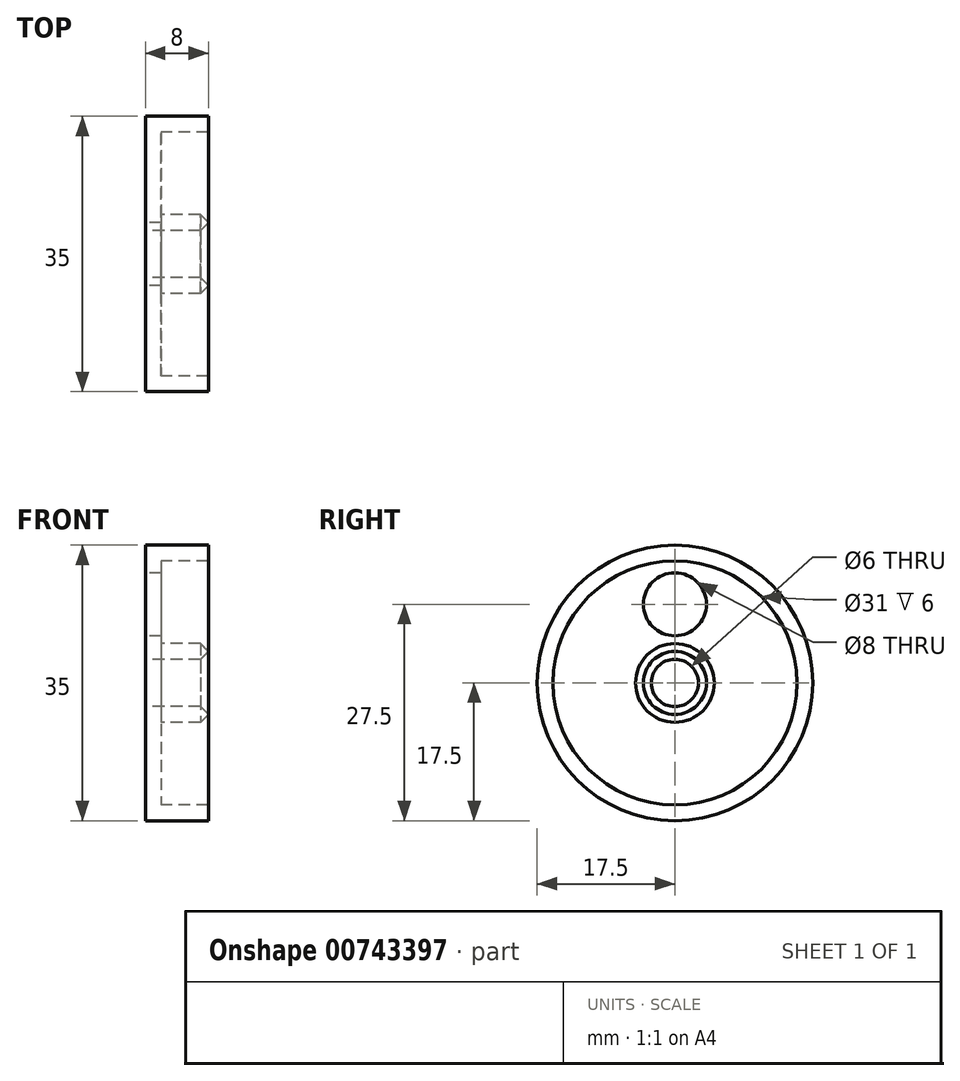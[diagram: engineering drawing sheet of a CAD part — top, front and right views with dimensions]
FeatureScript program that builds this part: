
annotation { "Feature Type Name" : "Feature", "Feature Type Description" : "" }
export const myFeature = defineFeature(function(context is Context, id is Id, definition is map)
    precondition{}
    {
        {
            var Q0;
            Q0=qCreatedBy(makeId("Front.planeOp"),FACE);
            var sketch = newSketch(context, id + "F0", { "sketchPlane" : qUnion([Q0])});
            skLineSegment(sketch, "E0.bottom", {"start": v(0, 0) * mm, "end": v(8, 0) * mm});
            skLineSegment(sketch, "E0.top", {"start": v(0, 17.5) * mm, "end": v(8, 17.5) * mm});
            skLineSegment(sketch, "E0.left", {"start": v(0, 0) * mm, "end": v(0, 17.5) * mm});
            skLineSegment(sketch, "E0.right", {"start": v(8, 0) * mm, "end": v(8, 17.5) * mm});
            skSolve(sketch);
        }
        {
            var Q0;
            Q0 = qSketchRegion(id + "F0", true);
            var Q1;
            Q1=sQuery(id+"F0.wireOp",EDGE,"E0.bottom");
            revolve(context, id + "F1", {"surfaceOperationType" : NewSurfaceOperationType.NEW, "entities" : qUnion([Q0]), "axis" : qUnion([Q1]), "revolveType" : RevolveType.FULL});
        }
        {
            var Q0;
            Q0=qCreatedBy(makeId("Right.planeOp"),FACE);
            var sketch = newSketch(context, id + "F2", { "sketchPlane" : qUnion([Q0])});
            skPoint(sketch, "E1", {"position": v(0, 0) * mm});
            skSolve(sketch);
        }
        {
            var Q0;
            Q0=sQuery(id+"F2.wireOp",VERTEX,"E1");
            var Q1;
            Q1=makeQuery(id+"F1.opRevolve","SWEPT_BODY",BODY,{"disambiguationData":[OSD([sQuery(id+"F0.wireOp",EDGE,"E0.bottom"),sQuery(id+"F0.wireOp",EDGE,"E0.top"),sQuery(id+"F0.wireOp",EDGE,"E0.left"),sQuery(id+"F0.wireOp",EDGE,"E0.right")])]});
            hole(context, id + "F3", {"style" : HoleStyle.SIMPLE, "endStyle" : HoleEndStyle.THROUGH, "oppositeDirection" : true, "holeDiameter" : 6 * mm, "majorDiameter" : 5 * mm, "isTappedThrough" : true, "tappedDepth" : 12 * mm, "tapClearance" : 3, "locations" : qUnion([Q0]), "scope" : qUnion([Q1])});
        }
        {
            var Q0;
            Q0=makeQuery(id+"F1.opRevolve","SWEPT_FACE",FACE,{"disambiguationData":[OSD([sQuery(id+"F0.wireOp",EDGE,"E0.right")])]});
            shell(context, id + "F4", {"entities" : qUnion([Q0]), "thickness" : 2 * mm});
        }
        {
            var Q0;
            Q0=qCreatedBy(makeId("Right.planeOp"),FACE);
            var sketch = newSketch(context, id + "F5", { "sketchPlane" : qUnion([Q0])});
            skPoint(sketch, "E2", {"position": v(0, 10) * mm});
            skSolve(sketch);
        }
        {
            var Q0;
            Q0=sQuery(id+"F5.wireOp",VERTEX,"E2");
            var Q1;
            Q1=makeQuery(id+"F1.opRevolve","SWEPT_BODY",BODY,{"disambiguationData":[OSD([sQuery(id+"F0.wireOp",EDGE,"E0.bottom"),sQuery(id+"F0.wireOp",EDGE,"E0.top"),sQuery(id+"F0.wireOp",EDGE,"E0.left"),sQuery(id+"F0.wireOp",EDGE,"E0.right")])]});
            hole(context, id + "F6", {"style" : HoleStyle.SIMPLE, "endStyle" : HoleEndStyle.THROUGH, "oppositeDirection" : true, "holeDiameter" : 8 * mm, "majorDiameter" : 5 * mm, "isTappedThrough" : true, "tappedDepth" : 12 * mm, "tapClearance" : 3, "locations" : qUnion([Q0]), "scope" : qUnion([Q1])});
        }
        {
            var Q0;
            Q0=makeQuery(id+"F4.opShell","OFFSET_FACE",FACE,{"disambiguationData":[OSD([sQuery(id+"F0.wireOp",EDGE,"E0.right")])]});
            chamfer(context, id + "F7", {"entities" : qUnion([Q0]), "width" : 1 * mm, "tangentPropagation" : true});
        }
    });
